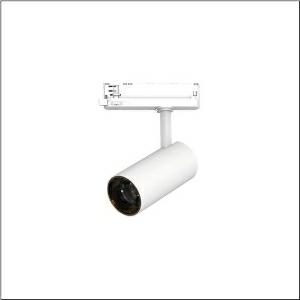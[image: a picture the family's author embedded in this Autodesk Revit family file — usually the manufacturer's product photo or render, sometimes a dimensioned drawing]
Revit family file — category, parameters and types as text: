
# Revit family: spot_31_slim_51sf137fa2b
name_source: partatom
category: Lighting Fixtures
units: mm (PartAtom-declared; Revit-internal decimal feet)

## family parameters
Cut with Voids When Loaded = No
Host = Face
Light Source = No
Part Type = Normal
Room Calculation Point = No
Round Connector Dimension = Use Diameter
Shared = No

## types (1)
- Spot 31 Slim (1 x LED, 2150 lm, 17.6 W, 2700K)
    Apparent Load = 18 VA
    CIE Flux Codes = 97 100 100 100 100
    Color Rendering = 90
    Color Temperature = 2700K
    Default Elevation = 1800 mm
    Description = Spot 31 Slim, directional spotlight, light control with reflector, of aluminium, LED rated luminous flux: 2.150lm, light colour: 927, control gear: ECG, with 3-phase adapter, mains connection: 220..240V, AC, 50/60Hz, housing, of aluminium, traffic white (RAL 9016), diameter: 70mm, adapter, of plastic, protection rating (complete): IP20, insulation class (complete): insulation class I (protective earthing), certification: CE, impact resistance: IK02, packaging unit: 1 piece
    Height = 210 mm
    Lamp = 1 x LED
    Lamp Light Flux = 2150 lm
    Lamp Power = 17.6 W
    Lamp count = 1
    Length = 70 mm
    Luminous efficacy = 122 lm/W
    Manufacturer = Siteco
    ModVariant = No
    Model = 51SF137FA2B
    Mounting Place = Ceiling
    Mounting Type = Pendant
    Number of Poles = 1
    OnlyDefault = Yes
    Power Factor = 1
    Product Name = Spot 31 Slim
    Product group = directional spotlight
    ProductGroupID = 905
    Protection Class = Protection class I
    Protection Degree = IP 20
    RLX_Detail_Level = 1
    RLX_Emergency_Light_Flux = 0 lm
    RLX_Emergency_Type = 0
    RLX_Emergency_Type_DB = No
    RlxData = <blob elided: 14149 chars, md5=bc148eb9>
    Socket = socket
    Standby Power = 0 W
    System Light Flux = 2150 lm
    System Power = 18 W
    Type Comments = Product without accessories
    Type Image = l_1228468.jpg
    URL = http://relux.com
    VarID = ---
    Voltage = 0 V
    Weight = 0.00 kg
    Width = 0 mm  [stored 0 ft]

note: [stored X ft] marks values corroborated as IEEE doubles in the binary element streams (Revit-internal decimal feet)

## geometry (parser evidence)
native form markers: Sweep x13
no freeform markers — native parametric forms only
